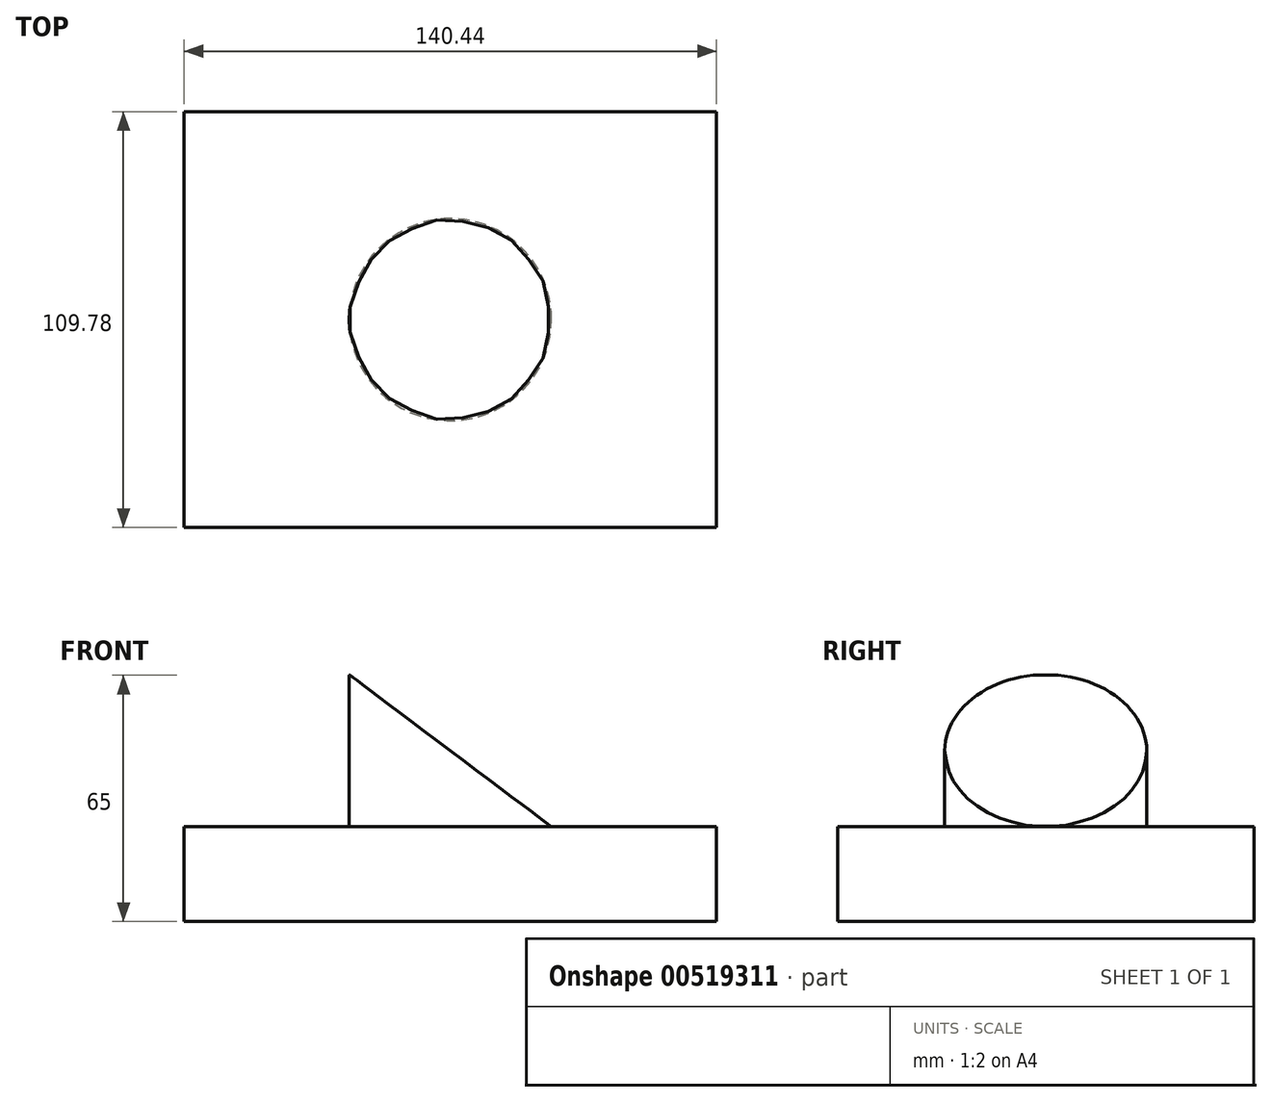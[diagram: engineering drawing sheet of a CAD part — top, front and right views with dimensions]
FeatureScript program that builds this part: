
annotation { "Feature Type Name" : "Feature", "Feature Type Description" : "" }
export const myFeature = defineFeature(function(context is Context, id is Id, definition is map)
    precondition{}
    {
        {
            var Q0;
            Q0=qCreatedBy(makeId("Top.planeOp"),FACE);
            var sketch = newSketch(context, id + "F0", { "sketchPlane" : qUnion([Q0])});
            skLineSegment(sketch, "E0.bottom", {"start": v(70.22, -54.9) * mm, "end": v(-70.22, -54.9) * mm});
            skLineSegment(sketch, "E0.top", {"start": v(70.22, 54.9) * mm, "end": v(-70.22, 54.9) * mm});
            skLineSegment(sketch, "E0.left", {"start": v(70.22, -54.9) * mm, "end": v(70.22, 54.9) * mm});
            skLineSegment(sketch, "E0.right", {"start": v(-70.22, -54.9) * mm, "end": v(-70.22, 54.9) * mm});
            skPoint(sketch, "E0.middle", {"position": v(0, 0) * mm});
            skSolve(sketch);
        }
        {
            var Q0;
            Q0=makeQuery(id+"F0.imprint","IMPRINT",FACE,{"disambiguationData":[TD([[makeQuery(id+"F0.imprint","IMPRINT",EDGE,{"derivedFrom":sQuery(id+"F0.wireOp",EDGE,"E0.bottom")}),-1.0]])]});
            extrude(context, id + "F1", {"entities" : qUnion([Q0]), "oppositeDirection" : true, "depth" : 25 * mm, "offsetDistance" : 25 * mm});
        }
        {
            var Q0;
            Q0=makeQuery(id+"F1.opExtrude","CAP_FACE",FACE,{"disambiguationData":[OSD([sQuery(id+"F0.wireOp",EDGE,"E0.bottom"),sQuery(id+"F0.wireOp",EDGE,"E0.top"),sQuery(id+"F0.wireOp",EDGE,"E0.left"),sQuery(id+"F0.wireOp",EDGE,"E0.right")])],"isStart":true});
            var sketch = newSketch(context, id + "F2", { "sketchPlane" : qUnion([Q0])});
            skCircle(sketch, "E1", {"center": v(0, 0) * mm, "radius": 26.67 * mm});
            skSolve(sketch);
        }
        {
            var Q0;
            Q0=makeQuery(id+"F2.imprint","IMPRINT",FACE,{"disambiguationData":[TD([[makeQuery(id+"F2.imprint","IMPRINT",EDGE,{"derivedFrom":sQuery(id+"F2.wireOp",EDGE,"E1")}),1.0]])]});
            extrude(context, id + "F3", {"entities" : qUnion([Q0]), "operationType" : NewBodyOperationType.ADD, "depth" : 40 * mm, "offsetDistance" : 25 * mm});
        }
        {
            var Q0;
            Q0=makeQuery(id+"F1.opExtrude","SWEPT_FACE",FACE,{"disambiguationData":[OSD([sQuery(id+"F0.wireOp",EDGE,"E0.bottom")])]});
            var sketch = newSketch(context, id + "F4", { "sketchPlane" : qUnion([Q0])});
            skLineSegment(sketch, "E2", {"start": v(26.69, 0) * mm, "end": v(26.69, 40.13) * mm});
            skLineSegment(sketch, "E3", {"start": v(26.69, 0) * mm, "end": v(-26.63, 40.13) * mm});
            skLineSegment(sketch, "E4", {"start": v(-26.63, 40.13) * mm, "end": v(26.69, 40.13) * mm});
            skSolve(sketch);
        }
        {
            var Q0;
            Q0=makeQuery(id+"F4.imprint","IMPRINT",FACE,{"disambiguationData":[TD([[makeQuery(id+"F4.imprint","IMPRINT",EDGE,{"derivedFrom":sQuery(id+"F4.wireOp",EDGE,"E2")}),1.0]])]});
            extrude(context, id + "F5", {"entities" : qUnion([Q0]), "operationType" : NewBodyOperationType.REMOVE, "oppositeDirection" : true, "depth" : 128 * mm, "offsetDistance" : 25 * mm});
        }
    });
